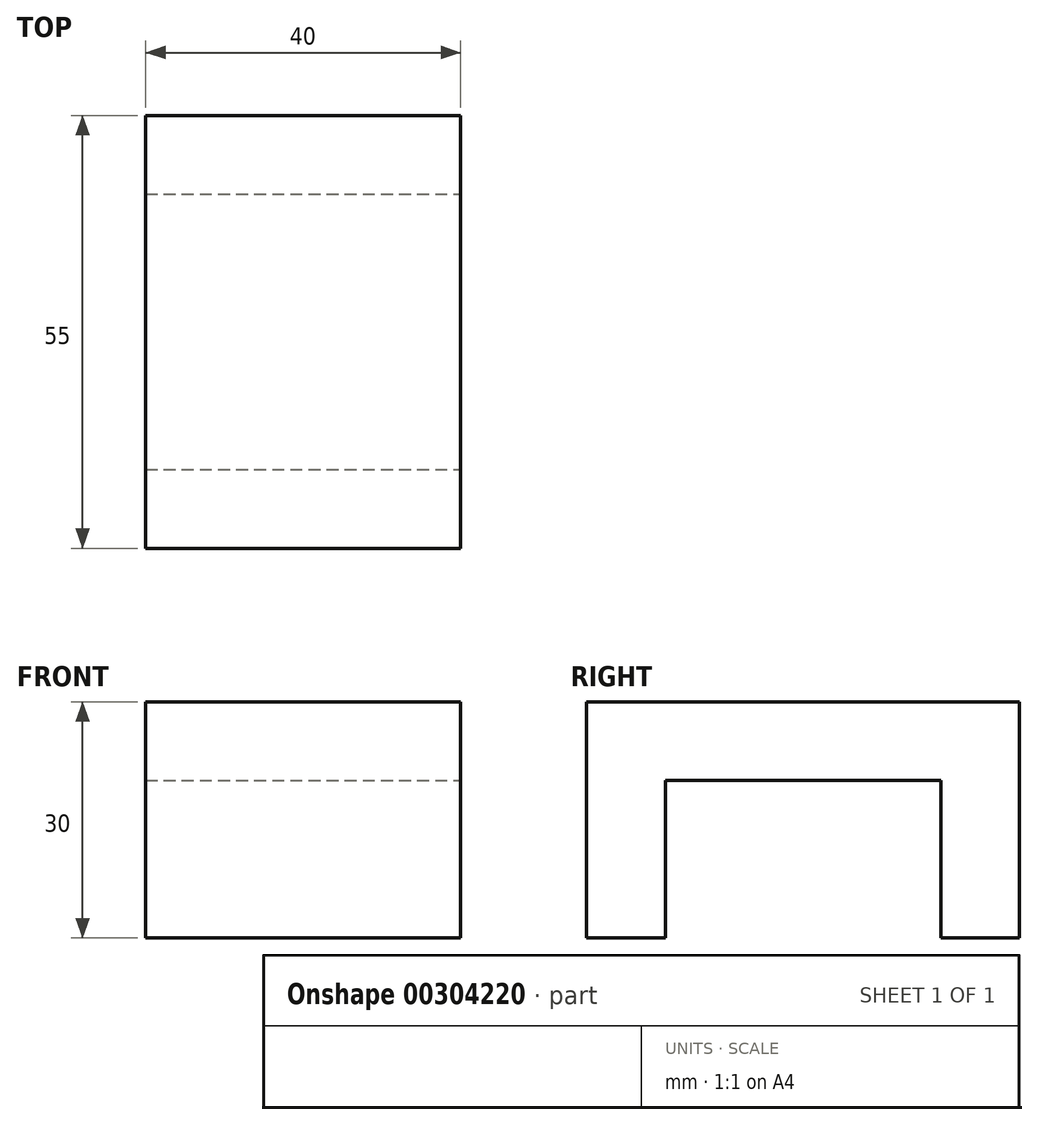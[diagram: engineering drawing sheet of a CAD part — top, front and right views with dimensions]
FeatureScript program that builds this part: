
annotation { "Feature Type Name" : "Feature", "Feature Type Description" : "" }
export const myFeature = defineFeature(function(context is Context, id is Id, definition is map)
    precondition{}
    {
        {
            var Q0;
            Q0=qCreatedBy(makeId("Top.planeOp"),FACE);
            var sketch = newSketch(context, id + "F0", { "sketchPlane" : qUnion([Q0])});
            skLineSegment(sketch, "E0.bottom", {"start": v(-20.33, 28.14) * mm, "end": v(19.67, 28.14) * mm});
            skLineSegment(sketch, "E0.top", {"start": v(-20.33, -26.86) * mm, "end": v(19.67, -26.86) * mm});
            skLineSegment(sketch, "E0.left", {"start": v(-20.33, 28.14) * mm, "end": v(-20.33, -26.86) * mm});
            skLineSegment(sketch, "E0.right", {"start": v(19.67, 28.14) * mm, "end": v(19.67, -26.86) * mm});
            skLineSegment(sketch, "E1.bottom", {"start": v(-20.33, 18.14) * mm, "end": v(19.67, 18.14) * mm});
            skLineSegment(sketch, "E1.top", {"start": v(-20.33, -16.86) * mm, "end": v(19.67, -16.86) * mm});
            skLineSegment(sketch, "E1.left", {"start": v(-20.33, 18.14) * mm, "end": v(-20.33, -16.86) * mm});
            skLineSegment(sketch, "E1.right", {"start": v(19.67, 18.14) * mm, "end": v(19.67, -16.86) * mm});
            skSolve(sketch);
        }
        {
            var Q0;
            Q0=makeQuery(id+"F0.imprint","IMPRINT",FACE,{"disambiguationData":[TD([[makeQuery(id+"F0.imprint","IMPRINT",EDGE,{"derivedFrom":sQuery(id+"F0.wireOp",EDGE,"E1.bottom")}),-1.0]])]});
            extrude(context, id + "F1", {"entities" : qUnion([Q0]), "depth" : 30 * mm});
        }
        {
            var Q0;
            Q0=qSketchRegion(id+"F0",true);
            extrude(context, id + "F2", {"entities" : qUnion([Q0]), "operationType" : NewBodyOperationType.ADD, "depth" : 30 * mm});
        }
        {
            var Q0;
            {var subQ0=sQuery(id+"F0.wireOp",EDGE,"E1.right");var subQ1=sQuery(id+"F0.wireOp",EDGE,"E1.left");Q0=makeQuery(id+"F2.boolean.opBoolean","MERGE",FACE,{"derivedFrom":[makeQuery(id+"F1.opExtrude","CAP_FACE",FACE,{"disambiguationData":[OSD([sQuery(id+"F0.wireOp",EDGE,"E1.bottom"),sQuery(id+"F0.wireOp",EDGE,"E1.top"),subQ1,subQ0])],"isStart":true}),makeQuery(id+"F2.opExtrude","CAP_FACE",FACE,{"disambiguationData":[OSD([sQuery(id+"F0.wireOp",EDGE,"E0.bottom"),sQuery(id+"F0.wireOp",EDGE,"E0.top"),sQuery(id+"F0.wireOp",EDGE,"E0.left"),sQuery(id+"F0.wireOp",EDGE,"E0.right"),subQ1,subQ0])],"isStart":true})]});}
            var sketch = newSketch(context, id + "F3", { "sketchPlane" : qUnion([Q0])});
            skLineSegment(sketch, "E2.bottom", {"start": v(-20.33, 16.86) * mm, "end": v(19.67, 16.86) * mm});
            skLineSegment(sketch, "E2.top", {"start": v(-20.33, -18.14) * mm, "end": v(19.67, -18.14) * mm});
            skLineSegment(sketch, "E2.left", {"start": v(-20.33, 16.86) * mm, "end": v(-20.33, -18.14) * mm});
            skLineSegment(sketch, "E2.right", {"start": v(19.67, 16.86) * mm, "end": v(19.67, -18.14) * mm});
            skSolve(sketch);
        }
        {
            var Q0;
            Q0=qSketchRegion(id+"F3",true);
            extrude(context, id + "F4", {"entities" : qUnion([Q0]), "operationType" : NewBodyOperationType.REMOVE, "oppositeDirection" : true, "depth" : 20 * mm});
        }
    });
